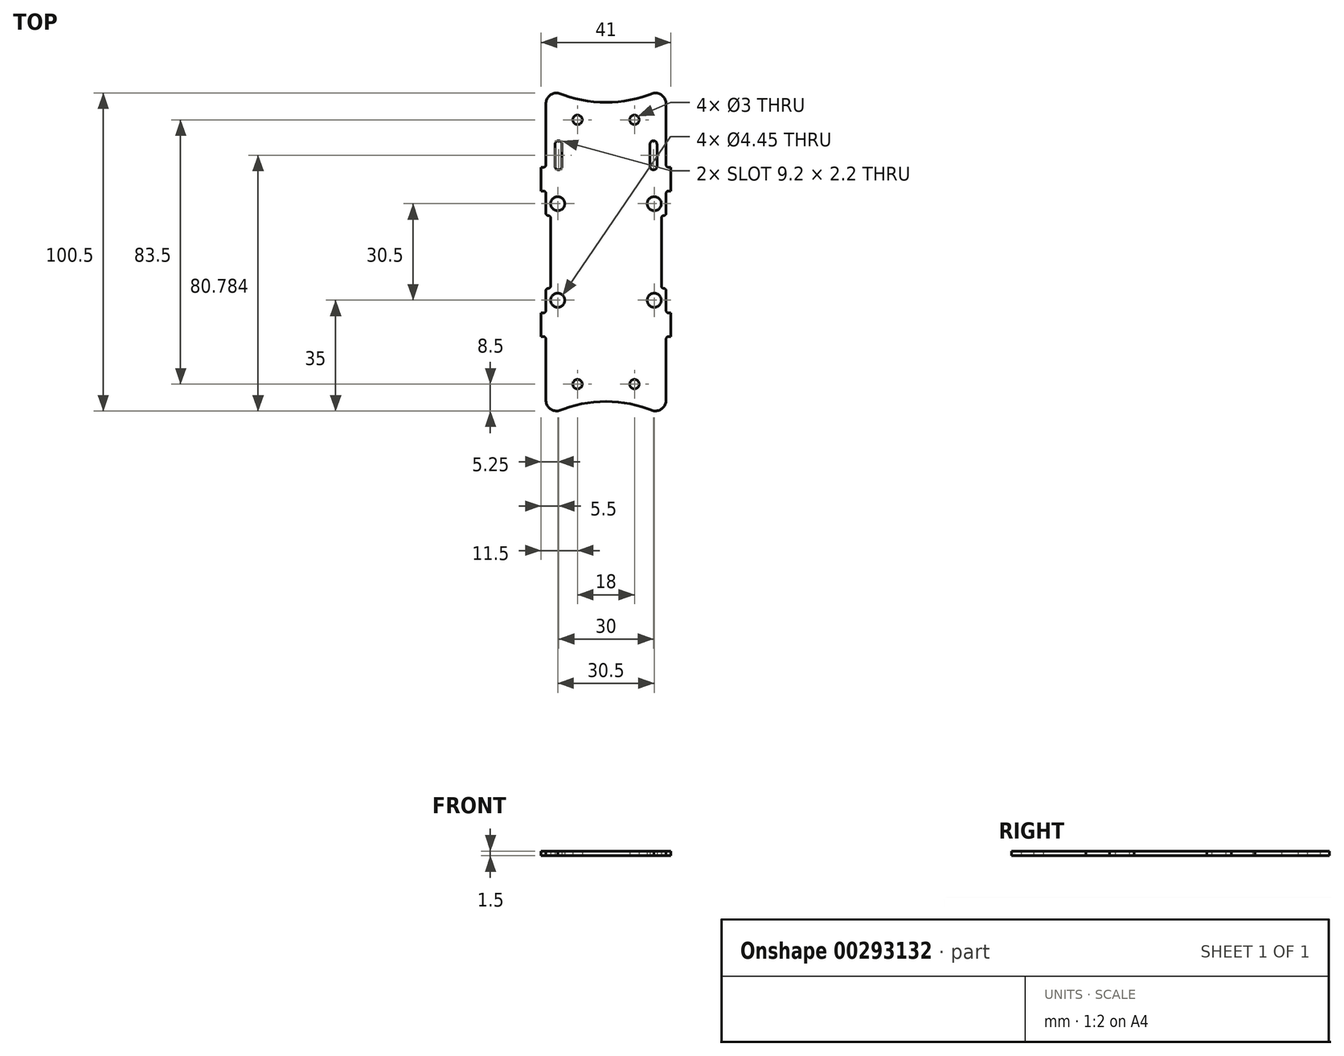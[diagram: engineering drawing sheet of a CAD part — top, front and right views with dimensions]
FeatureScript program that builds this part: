
annotation { "Feature Type Name" : "Feature", "Feature Type Description" : "" }
export const myFeature = defineFeature(function(context is Context, id is Id, definition is map)
    precondition{}
    {
        {
            var Q0;
            Q0=qCreatedBy(makeId("Top.planeOp"),FACE);
            var sketch = newSketch(context, id + "F0", { "sketchPlane" : qUnion([Q0])});
            skArc(sketch, "E0", {"start": v(19, -18.5) * mm, "mid": v(19.22, -19.03) * mm, "end": v(19.75, -19.25) * mm});
            skLineSegment(sketch, "E1", {"start": v(19.75, -19.25) * mm, "end": v(20.5, -19.25) * mm});
            skLineSegment(sketch, "E2", {"start": v(20.5, -19.25) * mm, "end": v(20.5, -26.75) * mm});
            skLineSegment(sketch, "E3", {"start": v(20.5, -26.75) * mm, "end": v(19.75, -26.75) * mm});
            skArc(sketch, "E4", {"start": v(19.75, -26.75) * mm, "mid": v(19.22, -26.97) * mm, "end": v(19, -27.5) * mm});
            skLineSegment(sketch, "E5", {"start": v(19, -27.5) * mm, "end": v(19, -46.75) * mm});
            skArc(sketch, "E6", {"start": v(15.5, -50.25) * mm, "mid": v(17.97, -49.22) * mm, "end": v(19, -46.75) * mm});
            skLineSegment(sketch, "E7", {"start": v(15.5, -50.25) * mm, "end": v(15.17, -50.25) * mm});
            skArc(sketch, "E8", {"start": v(15.17, -50.25) * mm, "mid": v(0, -47.25) * mm, "end": v(-15.17, -50.25) * mm});
            skLineSegment(sketch, "E9", {"start": v(-15.17, -50.25) * mm, "end": v(-15.5, -50.25) * mm});
            skArc(sketch, "E10", {"start": v(-19, -46.75) * mm, "mid": v(-17.97, -49.22) * mm, "end": v(-15.5, -50.25) * mm});
            skLineSegment(sketch, "E11", {"start": v(-19, -46.75) * mm, "end": v(-19, -27.5) * mm});
            skArc(sketch, "E12", {"start": v(-19, -27.5) * mm, "mid": v(-19.22, -26.97) * mm, "end": v(-19.75, -26.75) * mm});
            skLineSegment(sketch, "E13", {"start": v(-19.75, -26.75) * mm, "end": v(-20.5, -26.75) * mm});
            skLineSegment(sketch, "E14", {"start": v(-20.5, -26.75) * mm, "end": v(-20.5, -19.25) * mm});
            skLineSegment(sketch, "E15", {"start": v(-20.5, -19.25) * mm, "end": v(-19.75, -19.25) * mm});
            skArc(sketch, "E16", {"start": v(-19.75, -19.25) * mm, "mid": v(-19.22, -19.03) * mm, "end": v(-19, -18.5) * mm});
            skLineSegment(sketch, "E17", {"start": v(-19, -18.5) * mm, "end": v(-19, -12.25) * mm});
            skArc(sketch, "E18", {"start": v(-18.25, -11.5) * mm, "mid": v(-18.78, -11.72) * mm, "end": v(-19, -12.25) * mm});
            skArc(sketch, "E19", {"start": v(-18.25, -11.5) * mm, "mid": v(-17.72, -11.28) * mm, "end": v(-17.5, -10.75) * mm});
            skLineSegment(sketch, "E20", {"start": v(-17.5, -10.75) * mm, "end": v(-17.5, 10.75) * mm});
            skArc(sketch, "E21", {"start": v(-17.5, 10.75) * mm, "mid": v(-17.72, 11.28) * mm, "end": v(-18.25, 11.5) * mm});
            skArc(sketch, "E22", {"start": v(-19, 12.25) * mm, "mid": v(-18.78, 11.72) * mm, "end": v(-18.25, 11.5) * mm});
            skLineSegment(sketch, "E23", {"start": v(-19, 12.25) * mm, "end": v(-19, 18.5) * mm});
            skArc(sketch, "E24", {"start": v(-19, 18.5) * mm, "mid": v(-19.22, 19.03) * mm, "end": v(-19.75, 19.25) * mm});
            skLineSegment(sketch, "E25", {"start": v(-19.75, 19.25) * mm, "end": v(-20.5, 19.25) * mm});
            skLineSegment(sketch, "E26", {"start": v(-20.5, 19.25) * mm, "end": v(-20.5, 26.75) * mm});
            skLineSegment(sketch, "E27", {"start": v(-20.5, 26.75) * mm, "end": v(-19.75, 26.75) * mm});
            skArc(sketch, "E28", {"start": v(-19.75, 26.75) * mm, "mid": v(-19.22, 26.97) * mm, "end": v(-19, 27.5) * mm});
            skLineSegment(sketch, "E29", {"start": v(-19, 27.5) * mm, "end": v(-19, 46.75) * mm});
            skArc(sketch, "E30", {"start": v(-15.5, 50.25) * mm, "mid": v(-17.97, 49.22) * mm, "end": v(-19, 46.75) * mm});
            skLineSegment(sketch, "E31", {"start": v(-15.5, 50.25) * mm, "end": v(-15.17, 50.25) * mm});
            skArc(sketch, "E32", {"start": v(-15.17, 50.25) * mm, "mid": v(0, 47.25) * mm, "end": v(15.17, 50.25) * mm});
            skLineSegment(sketch, "E33", {"start": v(15.17, 50.25) * mm, "end": v(15.5, 50.25) * mm});
            skArc(sketch, "E34", {"start": v(19, 46.75) * mm, "mid": v(17.97, 49.22) * mm, "end": v(15.5, 50.25) * mm});
            skLineSegment(sketch, "E35", {"start": v(19, 46.75) * mm, "end": v(19, 27.5) * mm});
            skArc(sketch, "E36", {"start": v(19, 27.5) * mm, "mid": v(19.22, 26.97) * mm, "end": v(19.75, 26.75) * mm});
            skLineSegment(sketch, "E37", {"start": v(19.75, 26.75) * mm, "end": v(20.5, 26.75) * mm});
            skLineSegment(sketch, "E38", {"start": v(20.5, 26.75) * mm, "end": v(20.5, 19.25) * mm});
            skLineSegment(sketch, "E39", {"start": v(20.5, 19.25) * mm, "end": v(19.75, 19.25) * mm});
            skArc(sketch, "E40", {"start": v(19.75, 19.25) * mm, "mid": v(19.22, 19.03) * mm, "end": v(19, 18.5) * mm});
            skLineSegment(sketch, "E41", {"start": v(19, 18.5) * mm, "end": v(19, 12.25) * mm});
            skArc(sketch, "E42", {"start": v(18.25, 11.5) * mm, "mid": v(18.78, 11.72) * mm, "end": v(19, 12.25) * mm});
            skArc(sketch, "E43", {"start": v(18.25, 11.5) * mm, "mid": v(17.72, 11.28) * mm, "end": v(17.5, 10.75) * mm});
            skLineSegment(sketch, "E44", {"start": v(17.5, 10.75) * mm, "end": v(17.5, -10.75) * mm});
            skArc(sketch, "E45", {"start": v(17.5, -10.75) * mm, "mid": v(17.72, -11.28) * mm, "end": v(18.25, -11.5) * mm});
            skArc(sketch, "E46", {"start": v(19, -12.25) * mm, "mid": v(18.78, -11.72) * mm, "end": v(18.25, -11.5) * mm});
            skLineSegment(sketch, "E47", {"start": v(19, -12.25) * mm, "end": v(19, -18.5) * mm});
            skCircle(sketch, "E48", {"center": v(15.25, -15.25) * mm, "radius": 2.23 * mm});
            skCircle(sketch, "E49", {"center": v(15.25, 15.25) * mm, "radius": 2.23 * mm});
            skCircle(sketch, "E50", {"center": v(-15.25, 15.25) * mm, "radius": 2.23 * mm});
            skCircle(sketch, "E51", {"center": v(-15.25, -15.25) * mm, "radius": 2.23 * mm});
            skCircle(sketch, "E52", {"center": v(-9, -41.75) * mm, "radius": 1.5 * mm});
            skCircle(sketch, "E53", {"center": v(9, -41.75) * mm, "radius": 1.5 * mm});
            skCircle(sketch, "E54", {"center": v(9, 41.75) * mm, "radius": 1.5 * mm});
            skCircle(sketch, "E55", {"center": v(-9, 41.75) * mm, "radius": 1.5 * mm});
            skArc(sketch, "E56", {"start": v(-13.9, 34.03) * mm, "mid": v(-15, 35.13) * mm, "end": v(-16.1, 34.03) * mm});
            skLineSegment(sketch, "E57", {"start": v(-16.1, 27.03) * mm, "end": v(-16.1, 34.03) * mm});
            skArc(sketch, "E58", {"start": v(-16.1, 27.03) * mm, "mid": v(-15, 25.93) * mm, "end": v(-13.9, 27.03) * mm});
            skLineSegment(sketch, "E59", {"start": v(-13.9, 34.03) * mm, "end": v(-13.9, 27.03) * mm});
            skArc(sketch, "E60", {"start": v(16.1, 34.03) * mm, "mid": v(15, 35.13) * mm, "end": v(13.9, 34.03) * mm});
            skLineSegment(sketch, "E61", {"start": v(16.1, 27.03) * mm, "end": v(16.1, 34.03) * mm});
            skArc(sketch, "E62", {"start": v(13.9, 27.03) * mm, "mid": v(15, 25.93) * mm, "end": v(16.1, 27.03) * mm});
            skLineSegment(sketch, "E63", {"start": v(13.9, 34.03) * mm, "end": v(13.9, 27.03) * mm});
            skSolve(sketch);
        }
        {
            var Q0;
            Q0 = qSketchRegion(id + "F0", true);
            extrude(context, id + "F1", {"entities" : qUnion([Q0]), "depth" : 1.5 * mm});
        }
    });
